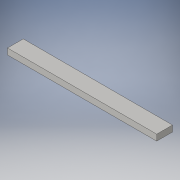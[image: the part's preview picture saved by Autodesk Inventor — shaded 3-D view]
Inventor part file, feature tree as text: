
AUTODESK INVENTOR PART (.ipt)
format: ipt  version: 2016 (Build 200138000, 138)  size: 89,600 bytes
history: native  units: in
note: dims shown in document units (in); Inventor stores cm internally (conversion verified against a paired STEP export)
features: extrude x1, sketch x1
ambient origin geometry x8: Origin, YZ Plane, XZ Plane, XY Plane, X Axis, Y Axis, Z Axis, Center Point
bodies: Body1 (feature_tree)
feature tree (2):
  extrude  "Extrusion3"  [1 undecoded]
  sketch  "Sketch4"  dims[d5=0.02in d6=0.0in]
note: 1 required parameter value undecoded (feature->parameter linkage not recoverable at this tier; creation-order binding heuristic only, values carry confidence <= 0.55)
